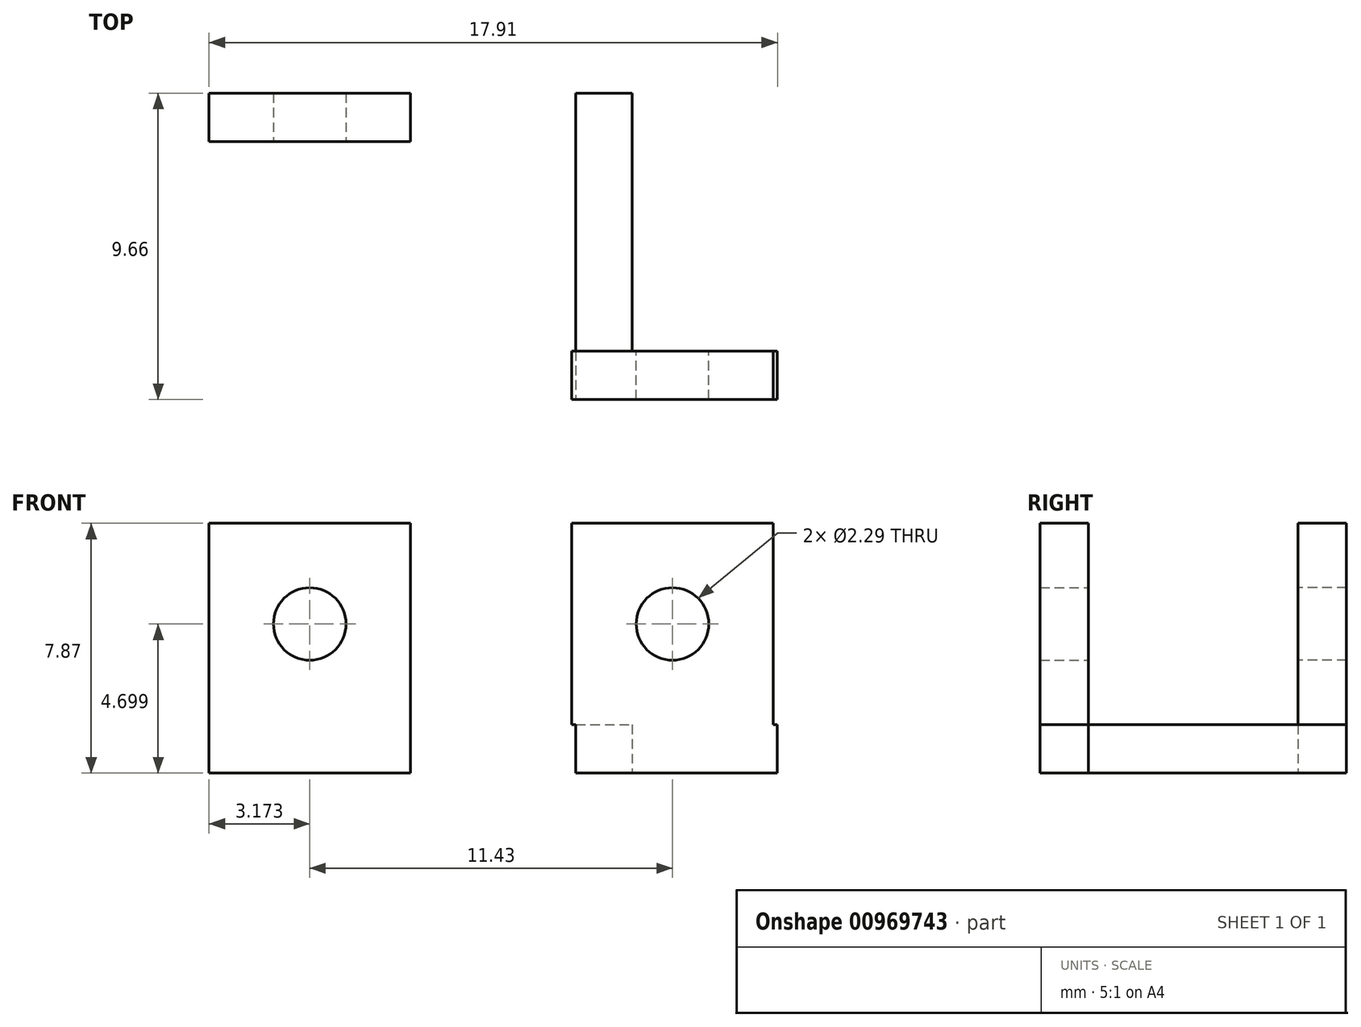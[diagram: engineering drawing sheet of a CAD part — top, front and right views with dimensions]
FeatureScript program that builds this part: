
annotation { "Feature Type Name" : "Feature", "Feature Type Description" : "" }
export const myFeature = defineFeature(function(context is Context, id is Id, definition is map)
    precondition{}
    {
        {
            var Q0;
            Q0=qCreatedBy(makeId("Top.planeOp"),FACE);
            var sketch = newSketch(context, id + "F0", { "sketchPlane" : qUnion([Q0])});
            skLineSegment(sketch, "E0.bottom", {"start": v(12.46, -4.83) * mm, "end": v(-12.46, -4.83) * mm});
            skLineSegment(sketch, "E0.top", {"start": v(0.87, 4.83) * mm, "end": v(-12.46, 4.83) * mm});
            skLineSegment(sketch, "E0.right", {"start": v(-12.46, -4.83) * mm, "end": v(-12.46, 4.83) * mm});
            skPoint(sketch, "E0.middle", {"position": v(0, 0) * mm});
            skLineSegment(sketch, "E1", {"start": v(0.87, 4.83) * mm, "end": v(0.87, -4.83) * mm});
            skLineSegment(sketch, "E2", {"start": v(0.87, 4.83) * mm, "end": v(12.46, -4.83) * mm});
            skLineSegment(sketch, "E3.bottom", {"start": v(-12.46, 4.83) * mm, "end": v(-6.11, 4.83) * mm});
            skLineSegment(sketch, "E3.top", {"start": v(-12.46, 3.3) * mm, "end": v(-6.11, 3.3) * mm});
            skLineSegment(sketch, "E3.left", {"start": v(-12.46, 4.83) * mm, "end": v(-12.46, 3.3) * mm});
            skLineSegment(sketch, "E3.right", {"start": v(-6.11, 4.83) * mm, "end": v(-6.11, 3.3) * mm});
            skLineSegment(sketch, "E4", {"start": v(-0.9, 4.83) * mm, "end": v(-0.9, -4.83) * mm});
            skLineSegment(sketch, "E5.bottom", {"start": v(0.87, -4.83) * mm, "end": v(7.23, -4.83) * mm});
            skLineSegment(sketch, "E5.left", {"start": v(0.87, -4.83) * mm, "end": v(0.87, -3.3) * mm});
            skLineSegment(sketch, "E6.bottom", {"start": v(-0.9, -4.83) * mm, "end": v(5.45, -4.83) * mm});
            skLineSegment(sketch, "E6.top", {"start": v(-0.9, -3.3) * mm, "end": v(5.45, -3.3) * mm});
            skLineSegment(sketch, "E6.left", {"start": v(-0.9, -4.83) * mm, "end": v(-0.9, -3.3) * mm});
            skLineSegment(sketch, "E6.right", {"start": v(5.45, -4.83) * mm, "end": v(5.45, -3.3) * mm});
            skSolve(sketch);
        }
        {
            var Q0;
            {var subQ0=sQuery(id+"F0.wireOp",EDGE,"E5.left");Q0=makeQuery(id+"F0.imprint","IMPRINT",FACE,{"disambiguationData":[TD([[makeQuery(id+"F0.imprint","IMPRINT",EDGE,{"derivedFrom":subQ0}),-1.0]])]});}
            var Q1;
            {var subQ0=sQuery(id+"F0.wireOp",EDGE,"E1");Q1=makeQuery(id+"F0.imprint","IMPRINT",FACE,{"disambiguationData":[TD([[makeQuery(id+"F0.imprint","IMPRINT",EDGE,{"derivedFrom":subQ0}),-1.0]])]});}
            var Q2;
            {var subQ0=sQuery(id+"F0.wireOp",EDGE,"E0.right");Q2=makeQuery(id+"F0.imprint","IMPRINT",FACE,{"disambiguationData":[TD([[makeQuery(id+"F0.imprint","IMPRINT",EDGE,{"derivedFrom":subQ0}),-1.0]])]});}
            var Q3;
            {var subQ3=sQuery(id+"F0.wireOp",EDGE,"E1");Q3=makeQuery(id+"F0.imprint","IMPRINT",FACE,{"disambiguationData":[TD([[makeQuery(id+"F0.imprint","IMPRINT",EDGE,{"derivedFrom":subQ3}),1.0]])]});}
            var Q4;
            Q4=makeQuery(id+"F0.imprint","IMPRINT",FACE,{"disambiguationData":[TD([[makeQuery(id+"F0.imprint","IMPRINT",EDGE,{"derivedFrom":sQuery(id+"F0.wireOp",EDGE,"E3.bottom")}),-1.0]])]});
            var Q5;
            {var subQ0=sQuery(id+"F0.wireOp",EDGE,"E5.left");Q5=makeQuery(id+"F0.imprint","IMPRINT",FACE,{"disambiguationData":[TD([[makeQuery(id+"F0.imprint","IMPRINT",EDGE,{"derivedFrom":subQ0}),1.0]])]});}
            extrude(context, id + "F1", {"entities" : qUnion([Q0, Q1, Q2, Q3, Q4, Q5]), "depth" : 1.52 * mm, "offsetDistance" : 25.4 * mm});
        }
        {
            var Q0;
            Q0=makeQuery(id+"F1.opExtrude","CAP_FACE",FACE,{"disambiguationData":[OSD([sQuery(id+"F0.wireOp",EDGE,"E0.bottom"),sQuery(id+"F0.wireOp",EDGE,"E0.top"),sQuery(id+"F0.wireOp",EDGE,"E0.right"),sQuery(id+"F0.wireOp",EDGE,"E2"),sQuery(id+"F0.wireOp",EDGE,"E3.bottom"),sQuery(id+"F0.wireOp",EDGE,"E3.left"),sQuery(id+"F0.wireOp",EDGE,"E5.bottom"),sQuery(id+"F0.wireOp",EDGE,"E6.bottom")])],"isStart":false});
            var sketch = newSketch(context, id + "F2", { "sketchPlane" : qUnion([Q0])});
            skLineSegment(sketch, "E7.bottom", {"start": v(-12.46, 4.83) * mm, "end": v(-6.11, 4.83) * mm});
            skLineSegment(sketch, "E7.top", {"start": v(-12.46, 3.3) * mm, "end": v(-6.11, 3.3) * mm});
            skLineSegment(sketch, "E7.left", {"start": v(-12.46, 4.83) * mm, "end": v(-12.46, 3.3) * mm});
            skLineSegment(sketch, "E7.right", {"start": v(-6.11, 4.83) * mm, "end": v(-6.11, 3.3) * mm});
            skLineSegment(sketch, "E8.bottom", {"start": v(-1.03, -4.83) * mm, "end": v(5.32, -4.83) * mm});
            skLineSegment(sketch, "E8.top", {"start": v(-1.03, -3.3) * mm, "end": v(5.32, -3.3) * mm});
            skLineSegment(sketch, "E8.left", {"start": v(-1.03, -4.83) * mm, "end": v(-1.03, -3.3) * mm});
            skLineSegment(sketch, "E8.right", {"start": v(5.32, -4.83) * mm, "end": v(5.32, -3.3) * mm});
            skSolve(sketch);
        }
        {
            var Q0;
            Q0=makeQuery(id+"F2.imprint","IMPRINT",FACE,{"disambiguationData":[TD([[makeQuery(id+"F2.imprint","IMPRINT",EDGE,{"derivedFrom":sQuery(id+"F2.wireOp",EDGE,"E7.bottom")}),1.0]])]});
            extrude(context, id + "F3", {"entities" : qUnion([Q0]), "operationType" : NewBodyOperationType.ADD, "depth" : 6.35 * mm, "offsetDistance" : 25.4 * mm});
        }
        {
            var Q0;
            Q0=makeQuery(id+"F3.opExtrude","SWEPT_FACE",FACE,{"disambiguationData":[OSD([sQuery(id+"F2.wireOp",EDGE,"E7.top")])]});
            var sketch = newSketch(context, id + "F4", { "sketchPlane" : qUnion([Q0])});
            skLineSegment(sketch, "E9", {"start": v(-12.46, 4.7) * mm, "end": v(-6.11, 4.7) * mm});
            skLineSegment(sketch, "E10", {"start": v(-9.29, 7.87) * mm, "end": v(-9.29, 1.52) * mm});
            skCircle(sketch, "E11", {"center": v(-9.29, 4.7) * mm, "radius": 1.14 * mm});
            skSolve(sketch);
        }
        {
            var Q0;
            {var subQ0=sQuery(id+"F4.wireOp",EDGE,"E10");var subQ1=sQuery(id+"F4.wireOp",EDGE,"E9");var subQ2=makeQuery(id+"F4.imprint","INTERSECT",VERTEX,{"derivedFrom":[subQ1,subQ0]});Q0=makeQuery(id+"F4.imprint","IMPRINT",FACE,{"disambiguationData":[TD([[makeQuery(id+"F4.imprint","IMPRINT",EDGE,{"disambiguationData":[TD([[subQ2,-1.0]])],"derivedFrom":subQ1}),1.0]])]});}
            var Q1;
            {var subQ0=sQuery(id+"F4.wireOp",EDGE,"E11");var subQ1=sQuery(id+"F4.wireOp",EDGE,"E9");var subQ2=makeQuery(id+"F4.imprint","INTERSECT",VERTEX,{"disambiguationData":[OD(0.0)],"derivedFrom":[subQ1,subQ0]});Q1=makeQuery(id+"F4.imprint","IMPRINT",FACE,{"disambiguationData":[TD([[makeQuery(id+"F4.imprint","IMPRINT",EDGE,{"disambiguationData":[TD([[subQ2,-1.0]])],"derivedFrom":subQ1}),1.0]])]});}
            var Q2;
            {var subQ0=sQuery(id+"F4.wireOp",EDGE,"E11");var subQ1=sQuery(id+"F4.wireOp",EDGE,"E9");var subQ2=makeQuery(id+"F4.imprint","INTERSECT",VERTEX,{"disambiguationData":[OD(0.0)],"derivedFrom":[subQ1,subQ0]});Q2=makeQuery(id+"F4.imprint","IMPRINT",FACE,{"disambiguationData":[TD([[makeQuery(id+"F4.imprint","IMPRINT",EDGE,{"disambiguationData":[TD([[subQ2,-1.0]])],"derivedFrom":subQ1}),-1.0]])]});}
            var Q3;
            {var subQ0=sQuery(id+"F4.wireOp",EDGE,"E10");var subQ1=sQuery(id+"F4.wireOp",EDGE,"E9");var subQ2=makeQuery(id+"F4.imprint","INTERSECT",VERTEX,{"derivedFrom":[subQ1,subQ0]});Q3=makeQuery(id+"F4.imprint","IMPRINT",FACE,{"disambiguationData":[TD([[makeQuery(id+"F4.imprint","IMPRINT",EDGE,{"disambiguationData":[TD([[subQ2,-1.0]])],"derivedFrom":subQ1}),-1.0]])]});}
            extrude(context, id + "F5", {"entities" : qUnion([Q0, Q1, Q2, Q3]), "operationType" : NewBodyOperationType.REMOVE, "oppositeDirection" : true, "depth" : 2.54 * mm, "offsetDistance" : 25.4 * mm});
        }
        {
            var Q0;
            Q0=makeQuery(id+"F2.imprint","IMPRINT",FACE,{"disambiguationData":[TD([[makeQuery(id+"F2.imprint","IMPRINT",EDGE,{"derivedFrom":sQuery(id+"F2.wireOp",EDGE,"E8.bottom")}),1.0]])]});
            extrude(context, id + "F6", {"entities" : qUnion([Q0]), "operationType" : NewBodyOperationType.ADD, "depth" : 6.35 * mm, "offsetDistance" : 25.4 * mm});
        }
        {
            var Q0;
            Q0=makeQuery(id+"F6.opExtrude","SWEPT_FACE",FACE,{"disambiguationData":[OSD([sQuery(id+"F2.wireOp",EDGE,"E8.top")])]});
            var sketch = newSketch(context, id + "F7", { "sketchPlane" : qUnion([Q0])});
            skLineSegment(sketch, "E12", {"start": v(1.03, 4.7) * mm, "end": v(-5.32, 4.7) * mm, "construction": true});
            skLineSegment(sketch, "E13", {"start": v(-2.14, 1.52) * mm, "end": v(-2.14, 7.87) * mm, "construction": true});
            skCircle(sketch, "E14", {"center": v(-2.14, 4.7) * mm, "radius": 1.14 * mm});
            skSolve(sketch);
        }
        {
            var Q0;
            Q0=makeQuery(id+"F7.imprint","IMPRINT",FACE,{"disambiguationData":[TD([[makeQuery(id+"F7.imprint","IMPRINT",EDGE,{"derivedFrom":sQuery(id+"F7.wireOp",EDGE,"E14")}),1.0]])]});
            extrude(context, id + "F8", {"entities" : qUnion([Q0]), "operationType" : NewBodyOperationType.REMOVE, "oppositeDirection" : true, "depth" : 2.54 * mm, "offsetDistance" : 25.4 * mm});
        }
    });
